# Revit family: PKFY-P63-100VKM-E
name_source: partatom
category: Mechanical Equipment
revit_build: Autodesk Revit Architecture 2012 (Build: 20110309_2315(x64)
units: mm (PartAtom-declared; Revit-internal decimal feet)

## types (8) — shared parameters
Connectable outdoor unit = R410A CITY MULTI
D = 295 mm  [stored 0.967848 ft]
Drain pipe_radius = 8 mm  [stored 0.0262467 ft]
External Material = Plastic,MUNSELL(1.0Y 9.2/0.2)
Fan Motor Output (kW) = 0.056
Fan_Quantity = 1
Fan_Type = Line flow fan
Gas pipe_radius = 7.9 mm
H = 365 mm  [stored 1.19751 ft]
Liquid pipe_radius = 4.8 mm
Manufacturer = Mitsubishi Electric Corporation
Phase = 1
Protection Device = Fuse
Refrigerant type = R401A
Space View = Yes
Subcategory = HVAC
URL = http://global.mitsubishielectric.com
Unit Weight (kg) = 21
W = 1170 mm  [stored 3.83858 ft]
zero-valued in all types: Maximum Circuit Ampacity (A), Maximum Overcurrent Protection (A), Refrigerant Charge (kg)

## per-type parameters (varying)
| type | Airflow Rate_High (cfm) | Airflow Rate_Low (cfm) | Cooling Capacity (BTU) | Cooling Current (A) | Cooling Power Input (kW) | Heating Capacity (BTU) | Heating Current (A) | Heating Power Input (kW) | Hertz | Model | Sound Pressure Level_High (dB(A)) | Sound Pressure Level_Low (dB(A)) | Voltage |
| PKFY-P63VKM-E_220V_50Hz | 706 | 565 | 24200 | 0.37 | 0.05 | 27300 | 0.3 | 0.04 | 50 | PKFY-P63VKM-E | 45 | 39 | 220 |
| PKFY-P100VKM-E_220V_50Hz | 918 | 706 | 38200 | 0.58 | 0.08 | 42600 | 0.51 | 0.07 | 50 | PKFY-P100VKM-E | 49 | 41 | 220 |
| PKFY-P100VKM-E_220V_60Hz | 918 | 706 | 38200 | 0.58 | 0.08 | 42600 | 0.51 | 0.07 | 60 | PKFY-P100VKM-E | 49 | 41 | 220 |
| PKFY-P100VKM-E_230V_50Hz | 918 | 706 | 38200 | 0.58 | 0.08 | 42600 | 0.51 | 0.07 | 50 | PKFY-P100VKM-E | 49 | 41 | 230 |
| PKFY-P100VKM-E_240V_50Hz | 918 | 706 | 38200 | 0.58 | 0.08 | 42600 | 0.51 | 0.07 | 50 | PKFY-P100VKM-E | 49 | 41 | 240 |
| PKFY-P63VKM-E_220V_60Hz | 706 | 565 | 24200 | 0.37 | 0.05 | 27300 | 0.3 | 0.04 | 60 | PKFY-P63VKM-E | 45 | 39 | 220 |
| PKFY-P63VKM-E_230V_50Hz | 706 | 565 | 24200 | 0.37 | 0.05 | 27300 | 0.3 | 0.04 | 50 | PKFY-P63VKM-E | 45 | 39 | 230 |
| PKFY-P63VKM-E_240V_50Hz | 706 | 565 | 24200 | 0.37 | 0.05 | 27300 | 0.3 | 0.04 | 50 | PKFY-P63VKM-E | 45 | 39 | 240 |

note: [stored X ft] marks values corroborated as IEEE doubles in the binary element streams (Revit-internal decimal feet)

## geometry (parser evidence)
native form markers: Blend x30
no freeform markers — native parametric forms only
